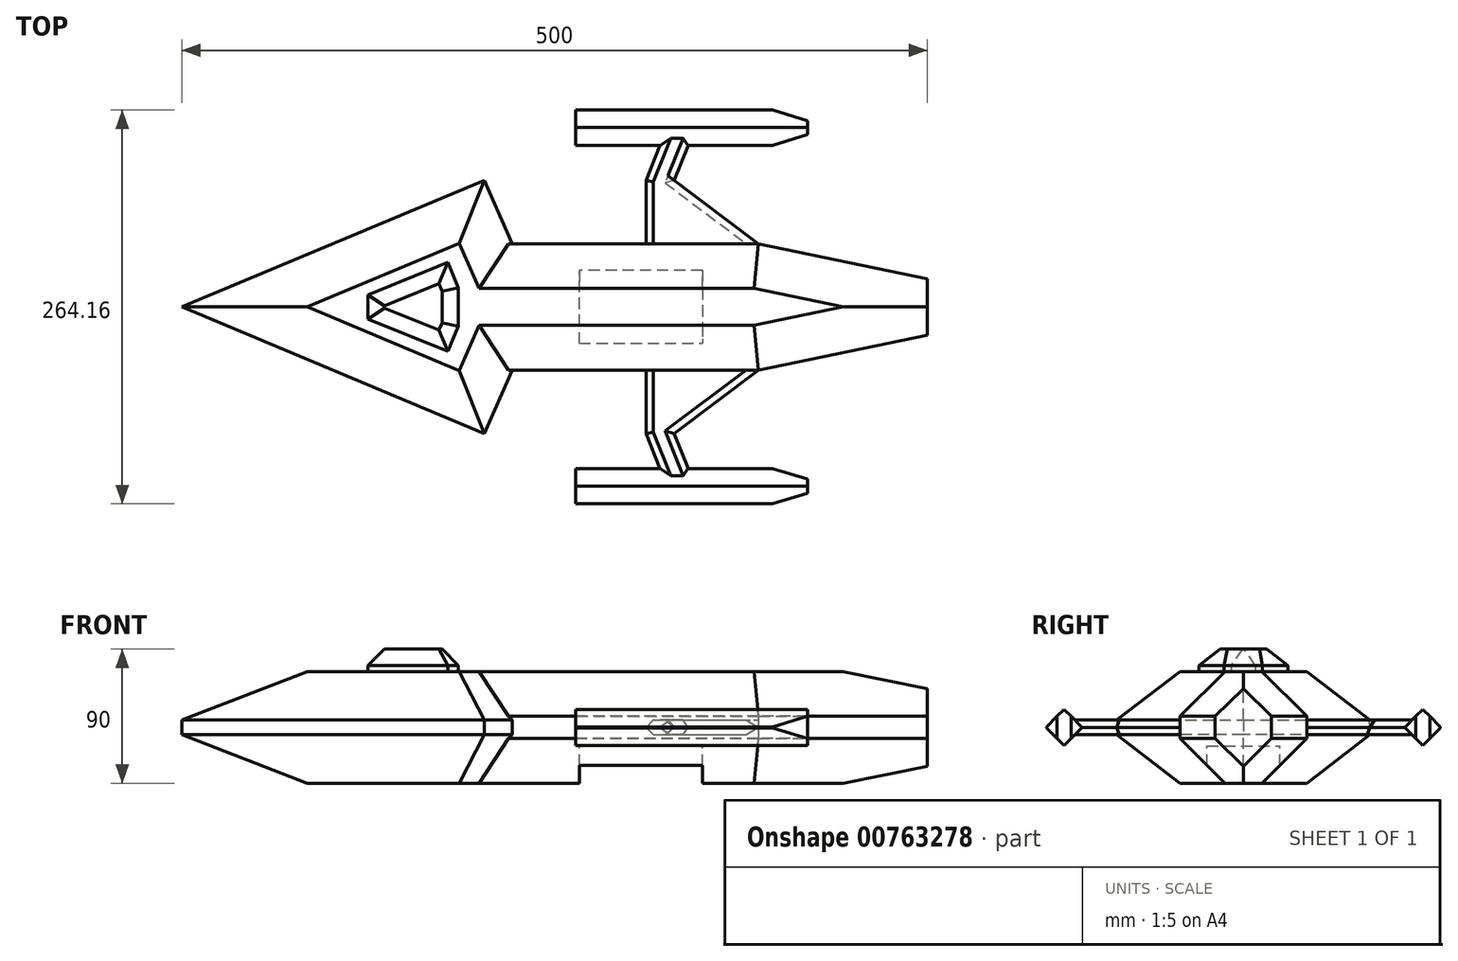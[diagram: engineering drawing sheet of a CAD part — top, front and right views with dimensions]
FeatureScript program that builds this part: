
annotation { "Feature Type Name" : "Feature", "Feature Type Description" : "" }
export const myFeature = defineFeature(function(context is Context, id is Id, definition is map)
    precondition{}
    {
        {
            var Q0;
            Q0=qCreatedBy(makeId("Top.planeOp"),FACE);
            var sketch = newSketch(context, id + "F0", { "sketchPlane" : qUnion([Q0])});
            skLineSegment(sketch, "E0", {"start": v(-309.49, 0) * mm, "end": v(-106.66, 84.9) * mm});
            skLineSegment(sketch, "E1", {"start": v(-106.66, 84.9) * mm, "end": v(-87.8, 42.45) * mm});
            skLineSegment(sketch, "E2", {"start": v(-87.8, 42.45) * mm, "end": v(1.83, 42.45) * mm});
            skLineSegment(sketch, "E3", {"start": v(1.83, 42.45) * mm, "end": v(1.83, 84.9) * mm});
            skLineSegment(sketch, "E4", {"start": v(1.83, 84.9) * mm, "end": v(11.27, 108.5) * mm});
            skLineSegment(sketch, "E5", {"start": v(11.27, 108.5) * mm, "end": v(-45.34, 108.5) * mm});
            skLineSegment(sketch, "E6", {"start": v(-45.34, 108.5) * mm, "end": v(-45.34, 132.08) * mm});
            skLineSegment(sketch, "E7", {"start": v(-45.34, 132.08) * mm, "end": v(86.74, 132.08) * mm});
            skLineSegment(sketch, "E8", {"start": v(86.74, 132.08) * mm, "end": v(110.32, 125) * mm});
            skLineSegment(sketch, "E9", {"start": v(110.32, 125) * mm, "end": v(110.32, 115.57) * mm});
            skLineSegment(sketch, "E10", {"start": v(110.32, 115.57) * mm, "end": v(86.74, 108.5) * mm});
            skLineSegment(sketch, "E11", {"start": v(86.74, 108.5) * mm, "end": v(30.13, 108.5) * mm});
            skLineSegment(sketch, "E12", {"start": v(30.13, 108.5) * mm, "end": v(20.7, 84.9) * mm});
            skLineSegment(sketch, "E13", {"start": v(20.7, 84.9) * mm, "end": v(77.3, 42.45) * mm});
            skLineSegment(sketch, "E14", {"start": v(77.3, 42.45) * mm, "end": v(190.51, 18.87) * mm});
            skLineSegment(sketch, "E15.MirrorCS", {"start": v(-309.49, 0) * mm, "end": v(-106.66, -84.9) * mm});
            skLineSegment(sketch, "E16.MirrorCS", {"start": v(-106.66, -84.9) * mm, "end": v(-87.8, -42.45) * mm});
            skLineSegment(sketch, "E17.MirrorCS", {"start": v(-87.8, -42.45) * mm, "end": v(1.83, -42.45) * mm});
            skLineSegment(sketch, "E18.MirrorCS", {"start": v(1.83, -42.45) * mm, "end": v(1.83, -84.9) * mm});
            skLineSegment(sketch, "E19.MirrorCS", {"start": v(1.83, -84.9) * mm, "end": v(11.27, -108.5) * mm});
            skLineSegment(sketch, "E20.MirrorCS", {"start": v(11.27, -108.5) * mm, "end": v(-45.34, -108.5) * mm});
            skLineSegment(sketch, "E21.MirrorCS", {"start": v(-45.34, -108.5) * mm, "end": v(-45.34, -132.08) * mm});
            skLineSegment(sketch, "E22.MirrorCS", {"start": v(-45.34, -132.08) * mm, "end": v(86.74, -132.08) * mm});
            skLineSegment(sketch, "E23.MirrorCS", {"start": v(86.74, -132.08) * mm, "end": v(110.32, -125) * mm});
            skLineSegment(sketch, "E24.MirrorCS", {"start": v(110.32, -125) * mm, "end": v(110.32, -115.57) * mm});
            skLineSegment(sketch, "E25.MirrorCS", {"start": v(110.32, -115.57) * mm, "end": v(86.74, -108.5) * mm});
            skLineSegment(sketch, "E26.MirrorCS", {"start": v(86.74, -108.5) * mm, "end": v(30.13, -108.5) * mm});
            skLineSegment(sketch, "E27.MirrorCS", {"start": v(30.13, -108.5) * mm, "end": v(20.7, -84.9) * mm});
            skLineSegment(sketch, "E28.MirrorCS", {"start": v(20.7, -84.9) * mm, "end": v(77.3, -42.45) * mm});
            skLineSegment(sketch, "E29.MirrorCS", {"start": v(77.3, -42.45) * mm, "end": v(190.51, -18.87) * mm});
            skLineSegment(sketch, "E30", {"start": v(190.51, -18.87) * mm, "end": v(190.51, 18.87) * mm});
            skPoint(sketch, "E31.endSnap0", {"position": v(98.53, 112.03) * mm});
            skPoint(sketch, "E32.startSnap0", {"position": v(-208.07, 42.45) * mm});
            skPoint(sketch, "E32.endSnap0", {"position": v(-208.07, 42.45) * mm});
            skPoint(sketch, "E33.endSnap0", {"position": v(-117.98, 30.43) * mm});
            skLineSegment(sketch, "E34", {"start": v(11.27, 108.5) * mm, "end": v(30.13, 108.5) * mm});
            skLineSegment(sketch, "E35", {"start": v(11.27, -108.5) * mm, "end": v(30.13, -108.5) * mm});
            skLineSegment(sketch, "E36", {"start": v(1.83, -42.45) * mm, "end": v(77.3, -42.45) * mm});
            skLineSegment(sketch, "E37", {"start": v(1.83, 42.45) * mm, "end": v(77.3, 42.45) * mm});
            skSolve(sketch);
        }
        {
            var Q0;
            Q0=makeQuery(id+"F0.imprint","IMPRINT",FACE,{"disambiguationData":[TD([[makeQuery(id+"F0.imprint","IMPRINT",EDGE,{"derivedFrom":sQuery(id+"F0.wireOp",EDGE,"E33")}),-1.0]])]});
            var Q1;
            Q1=makeQuery(id+"F0.imprint","IMPRINT",FACE,{"disambiguationData":[TD([[makeQuery(id+"F0.imprint","IMPRINT",EDGE,{"derivedFrom":sQuery(id+"F0.wireOp",EDGE,"E31")}),-1.0]])]});
            var Q2;
            Q2=makeQuery(id+"F0.imprint","IMPRINT",FACE,{"disambiguationData":[TD([[makeQuery(id+"F0.imprint","IMPRINT",EDGE,{"derivedFrom":sQuery(id+"F0.wireOp",EDGE,"E0")}),-1.0]])]});
            extrude(context, id + "F1", {"entities" : qUnion([Q0, Q1, Q2]), "depth" : 75 * mm, "offsetDistance" : 25 * mm, "symmetric" : true});
        }
        {
            var Q0;
            Q0=makeQuery(id+"F1.opExtrude","CAP_EDGE",EDGE,{"disambiguationData":[OSD([sQuery(id+"F0.wireOp",EDGE,"E0")])],"isStart":true});
            var Q1;
            Q1=makeQuery(id+"F1.opExtrude","CAP_EDGE",EDGE,{"disambiguationData":[OSD([sQuery(id+"F0.wireOp",EDGE,"E0")])],"isStart":false});
            var Q2;
            Q2=makeQuery(id+"F1.opExtrude","CAP_EDGE",EDGE,{"disambiguationData":[OSD([sQuery(id+"F0.wireOp",EDGE,"E15.MirrorCS")])],"isStart":false});
            var Q3;
            Q3=makeQuery(id+"F1.opExtrude","CAP_EDGE",EDGE,{"disambiguationData":[OSD([sQuery(id+"F0.wireOp",EDGE,"E15.MirrorCS")])],"isStart":true});
            var Q4;
            Q4=makeQuery(id+"F1.opExtrude","CAP_EDGE",EDGE,{"disambiguationData":[OSD([sQuery(id+"F0.wireOp",EDGE,"E16.MirrorCS")])],"isStart":false});
            var Q5;
            Q5=makeQuery(id+"F1.opExtrude","CAP_EDGE",EDGE,{"disambiguationData":[OSD([sQuery(id+"F0.wireOp",EDGE,"E16.MirrorCS")])],"isStart":true});
            var Q6;
            Q6=makeQuery(id+"F1.opExtrude","CAP_EDGE",EDGE,{"disambiguationData":[OSD([sQuery(id+"F0.wireOp",EDGE,"E1")])],"isStart":false});
            var Q7;
            Q7=makeQuery(id+"F1.opExtrude","CAP_EDGE",EDGE,{"disambiguationData":[OSD([sQuery(id+"F0.wireOp",EDGE,"E1")])],"isStart":true});
            chamfer(context, id + "F2", {"entities" : qUnion([Q0, Q1, Q2, Q3, Q4, Q5, Q6, Q7]), "width" : 32.5 * mm, "tangentPropagation" : true});
        }
        {
            var Q0;
            Q0=makeQuery(id+"F0.imprint","IMPRINT",FACE,{"disambiguationData":[TD([[makeQuery(id+"F0.imprint","IMPRINT",EDGE,{"derivedFrom":sQuery(id+"F0.wireOp",EDGE,"E18.MirrorCS")}),1.0]])]});
            var Q1;
            Q1=makeQuery(id+"F0.imprint","IMPRINT",FACE,{"disambiguationData":[TD([[makeQuery(id+"F0.imprint","IMPRINT",EDGE,{"derivedFrom":sQuery(id+"F0.wireOp",EDGE,"E3")}),-1.0]])]});
            extrude(context, id + "F3", {"entities" : qUnion([Q0, Q1]), "operationType" : NewBodyOperationType.ADD, "depth" : 10 * mm, "offsetDistance" : 25 * mm, "symmetric" : true});
        }
        {
            var Q0;
            Q0=makeQuery(id+"F0.imprint","IMPRINT",FACE,{"disambiguationData":[TD([[makeQuery(id+"F0.imprint","IMPRINT",EDGE,{"derivedFrom":sQuery(id+"F0.wireOp",EDGE,"E5")}),-1.0]])]});
            var Q1;
            Q1=makeQuery(id+"F0.imprint","IMPRINT",FACE,{"disambiguationData":[TD([[makeQuery(id+"F0.imprint","IMPRINT",EDGE,{"derivedFrom":sQuery(id+"F0.wireOp",EDGE,"E20.MirrorCS")}),1.0]])]});
            extrude(context, id + "F4", {"entities" : qUnion([Q0, Q1]), "operationType" : NewBodyOperationType.ADD, "depth" : 25 * mm, "offsetDistance" : 25 * mm, "symmetric" : true});
        }
        {
            var Q0;
            Q0=makeQuery(id+"F1.opExtrude","CAP_EDGE",EDGE,{"disambiguationData":[OSD([sQuery(id+"F0.wireOp",EDGE,"E14")])],"isStart":true});
            var Q1;
            Q1=makeQuery(id+"F1.opExtrude","CAP_EDGE",EDGE,{"disambiguationData":[OSD([sQuery(id+"F0.wireOp",EDGE,"E14")])],"isStart":false});
            var Q2;
            Q2=makeQuery(id+"F1.opExtrude","CAP_EDGE",EDGE,{"disambiguationData":[OSD([sQuery(id+"F0.wireOp",EDGE,"E29.MirrorCS")])],"isStart":false});
            var Q3;
            Q3=makeQuery(id+"F1.opExtrude","CAP_EDGE",EDGE,{"disambiguationData":[OSD([sQuery(id+"F0.wireOp",EDGE,"E29.MirrorCS")])],"isStart":true});
            var Q4;
            Q4=makeQuery(id+"F1.opExtrude","CAP_EDGE",EDGE,{"disambiguationData":[OSD([sQuery(id+"F0.wireOp",EDGE,"E17.MirrorCS"),sQuery(id+"F0.wireOp",EDGE,"E36")])],"isStart":true});
            var Q5;
            Q5=makeQuery(id+"F1.opExtrude","CAP_EDGE",EDGE,{"disambiguationData":[OSD([sQuery(id+"F0.wireOp",EDGE,"E17.MirrorCS"),sQuery(id+"F0.wireOp",EDGE,"E36")])],"isStart":false});
            var Q6;
            Q6=makeQuery(id+"F1.opExtrude","CAP_EDGE",EDGE,{"disambiguationData":[OSD([sQuery(id+"F0.wireOp",EDGE,"E2"),sQuery(id+"F0.wireOp",EDGE,"E37")])],"isStart":true});
            var Q7;
            Q7=makeQuery(id+"F1.opExtrude","CAP_EDGE",EDGE,{"disambiguationData":[OSD([sQuery(id+"F0.wireOp",EDGE,"E2"),sQuery(id+"F0.wireOp",EDGE,"E37")])],"isStart":false});
            chamfer(context, id + "F5", {"entities" : qUnion([Q0, Q1, Q2, Q3, Q4, Q5, Q6, Q7]), "width" : 30 * mm, "tangentPropagation" : true});
        }
        {
            var Q0;
            Q0=makeQuery(id+"F3.opExtrude","CAP_EDGE",EDGE,{"disambiguationData":[OSD([sQuery(id+"F0.wireOp",EDGE,"E3")])],"isStart":false});
            var Q1;
            Q1=makeQuery(id+"F3.opExtrude","CAP_EDGE",EDGE,{"disambiguationData":[OSD([sQuery(id+"F0.wireOp",EDGE,"E3")])],"isStart":true});
            var Q2;
            Q2=makeQuery(id+"F3.opExtrude","CAP_EDGE",EDGE,{"disambiguationData":[OSD([sQuery(id+"F0.wireOp",EDGE,"E13")])],"isStart":true});
            var Q3;
            Q3=makeQuery(id+"F3.opExtrude","CAP_EDGE",EDGE,{"disambiguationData":[OSD([sQuery(id+"F0.wireOp",EDGE,"E4")])],"isStart":false});
            var Q4;
            Q4=makeQuery(id+"F3.opExtrude","CAP_EDGE",EDGE,{"disambiguationData":[OSD([sQuery(id+"F0.wireOp",EDGE,"E4")])],"isStart":true});
            var Q5;
            Q5=makeQuery(id+"F3.opExtrude","CAP_EDGE",EDGE,{"disambiguationData":[OSD([sQuery(id+"F0.wireOp",EDGE,"E12")])],"isStart":true});
            var Q6;
            Q6=makeQuery(id+"F3.opExtrude","CAP_EDGE",EDGE,{"disambiguationData":[OSD([sQuery(id+"F0.wireOp",EDGE,"E12")])],"isStart":false});
            var Q7;
            Q7=makeQuery(id+"F3.opExtrude","CAP_EDGE",EDGE,{"disambiguationData":[OSD([sQuery(id+"F0.wireOp",EDGE,"E28.MirrorCS")])],"isStart":true});
            var Q8;
            Q8=makeQuery(id+"F3.opExtrude","CAP_EDGE",EDGE,{"disambiguationData":[OSD([sQuery(id+"F0.wireOp",EDGE,"E18.MirrorCS")])],"isStart":true});
            var Q9;
            Q9=makeQuery(id+"F3.opExtrude","CAP_EDGE",EDGE,{"disambiguationData":[OSD([sQuery(id+"F0.wireOp",EDGE,"E19.MirrorCS")])],"isStart":true});
            var Q10;
            Q10=makeQuery(id+"F3.opExtrude","CAP_EDGE",EDGE,{"disambiguationData":[OSD([sQuery(id+"F0.wireOp",EDGE,"E27.MirrorCS")])],"isStart":true});
            var Q11;
            Q11=makeQuery(id+"F3.opExtrude","CAP_EDGE",EDGE,{"disambiguationData":[OSD([sQuery(id+"F0.wireOp",EDGE,"E18.MirrorCS")])],"isStart":false});
            var Q12;
            Q12=makeQuery(id+"F3.opExtrude","CAP_EDGE",EDGE,{"disambiguationData":[OSD([sQuery(id+"F0.wireOp",EDGE,"E19.MirrorCS")])],"isStart":false});
            var Q13;
            Q13=makeQuery(id+"F3.opExtrude","CAP_EDGE",EDGE,{"disambiguationData":[OSD([sQuery(id+"F0.wireOp",EDGE,"E28.MirrorCS")])],"isStart":false});
            var Q14;
            Q14=makeQuery(id+"F3.opExtrude","CAP_EDGE",EDGE,{"disambiguationData":[OSD([sQuery(id+"F0.wireOp",EDGE,"E27.MirrorCS")])],"isStart":false});
            chamfer(context, id + "F6", {"entities" : qUnion([Q0, Q1, Q2, Q3, Q4, Q5, Q6, Q7, Q8, Q9, Q10, Q11, Q12, Q13, Q14]), "width" : 5 * mm, "tangentPropagation" : true});
        }
        {
            var Q0;
            Q0=makeQuery(id+"F4.opExtrude","CAP_EDGE",EDGE,{"disambiguationData":[OSD([sQuery(id+"F0.wireOp",EDGE,"E22.MirrorCS")])],"isStart":false});
            var Q1;
            Q1=makeQuery(id+"F4.opExtrude","CAP_EDGE",EDGE,{"disambiguationData":[OSD([sQuery(id+"F0.wireOp",EDGE,"E20.MirrorCS"),sQuery(id+"F0.wireOp",EDGE,"E26.MirrorCS"),sQuery(id+"F0.wireOp",EDGE,"E35")])],"isStart":false});
            var Q2;
            Q2=makeQuery(id+"F4.opExtrude","CAP_EDGE",EDGE,{"disambiguationData":[OSD([sQuery(id+"F0.wireOp",EDGE,"E22.MirrorCS")])],"isStart":true});
            var Q3;
            Q3=makeQuery(id+"F4.opExtrude","CAP_EDGE",EDGE,{"disambiguationData":[OSD([sQuery(id+"F0.wireOp",EDGE,"E20.MirrorCS"),sQuery(id+"F0.wireOp",EDGE,"E26.MirrorCS"),sQuery(id+"F0.wireOp",EDGE,"E35")])],"isStart":true});
            var Q4;
            Q4=makeQuery(id+"F4.opExtrude","CAP_EDGE",EDGE,{"disambiguationData":[OSD([sQuery(id+"F0.wireOp",EDGE,"E7")])],"isStart":true});
            var Q5;
            Q5=makeQuery(id+"F4.opExtrude","CAP_EDGE",EDGE,{"disambiguationData":[OSD([sQuery(id+"F0.wireOp",EDGE,"E7")])],"isStart":false});
            var Q6;
            Q6=makeQuery(id+"F4.opExtrude","CAP_EDGE",EDGE,{"disambiguationData":[OSD([sQuery(id+"F0.wireOp",EDGE,"E5"),sQuery(id+"F0.wireOp",EDGE,"E11"),sQuery(id+"F0.wireOp",EDGE,"E34")])],"isStart":false});
            var Q7;
            Q7=makeQuery(id+"F4.opExtrude","CAP_EDGE",EDGE,{"disambiguationData":[OSD([sQuery(id+"F0.wireOp",EDGE,"E5"),sQuery(id+"F0.wireOp",EDGE,"E11"),sQuery(id+"F0.wireOp",EDGE,"E34")])],"isStart":true});
            chamfer(context, id + "F7", {"entities" : qUnion([Q0, Q1, Q2, Q3, Q4, Q5, Q6, Q7]), "width" : 12.2 * mm, "tangentPropagation" : true});
        }
        {
            var Q0;
            Q0=qCreatedBy(makeId("Top.planeOp"),FACE);
            cPlane(context, id + "F8", {"entities" : qUnion([Q0]), "cplaneType" : CPlaneType.OFFSET, "offset" : 37.5 * mm, "width" : 150 * mm, "height" : 150 * mm});
        }
        {
            var Q0;
            Q0=qCreatedBy(id+"F8.planeOp",FACE);
            var sketch = newSketch(context, id + "F9", { "sketchPlane" : qUnion([Q0])});
            skLineSegment(sketch, "E38", {"start": v(-184.6, -8.14) * mm, "end": v(-130.94, -29.85) * mm});
            skLineSegment(sketch, "E39", {"start": v(-130.94, -29.85) * mm, "end": v(-124.05, -12.82) * mm});
            skLineSegment(sketch, "E40.MirrorCS", {"start": v(-130.94, 29.85) * mm, "end": v(-124.05, 12.82) * mm});
            skLineSegment(sketch, "E41.MirrorCS", {"start": v(-184.6, 8.14) * mm, "end": v(-130.94, 29.85) * mm});
            skLineSegment(sketch, "E42", {"start": v(-184.6, -8.14) * mm, "end": v(-184.6, 8.14) * mm});
            skLineSegment(sketch, "E43", {"start": v(-124.05, -12.82) * mm, "end": v(-124.05, 12.82) * mm});
            skSolve(sketch);
        }
        {
            var Q0;
            Q0=makeQuery(id+"F9.imprint","IMPRINT",FACE,{"disambiguationData":[TD([[makeQuery(id+"F9.imprint","IMPRINT",EDGE,{"derivedFrom":sQuery(id+"F9.wireOp",EDGE,"E38")}),1.0]])]});
            extrude(context, id + "F10", {"entities" : qUnion([Q0]), "operationType" : NewBodyOperationType.ADD, "depth" : 15 * mm, "offsetDistance" : 25 * mm});
        }
        {
            var Q0;
            Q0=makeQuery(id+"F10.opExtrude","CAP_FACE",FACE,{"disambiguationData":[OSD([sQuery(id+"F9.wireOp",EDGE,"E38"),sQuery(id+"F9.wireOp",EDGE,"E39"),sQuery(id+"F9.wireOp",EDGE,"E40.MirrorCS"),sQuery(id+"F9.wireOp",EDGE,"E41.MirrorCS"),sQuery(id+"F9.wireOp",EDGE,"E42"),sQuery(id+"F9.wireOp",EDGE,"E43")])],"isStart":false});
            chamfer(context, id + "F11", {"entities" : qUnion([Q0]), "width" : 11 * mm, "tangentPropagation" : true});
        }
        {
            var Q0;
            Q0=qCreatedBy(makeId("Top.planeOp"),FACE);
            cPlane(context, id + "F12", {"entities" : qUnion([Q0]), "cplaneType" : CPlaneType.OFFSET, "offset" : 12.5 * mm, "oppositeDirection" : true, "width" : 150 * mm, "height" : 150 * mm});
        }
        {
            var Q0;
            Q0=qCreatedBy(id+"F12.planeOp",FACE);
            var sketch = newSketch(context, id + "F13", { "sketchPlane" : qUnion([Q0])});
            skLineSegment(sketch, "E44", {"start": v(-42.9, 24.42) * mm, "end": v(39.7, 24.42) * mm});
            skLineSegment(sketch, "E45.MirrorCS", {"start": v(-42.9, -24.42) * mm, "end": v(39.7, -24.42) * mm});
            skLineSegment(sketch, "E46", {"start": v(-42.9, -24.42) * mm, "end": v(-42.9, 24.42) * mm});
            skLineSegment(sketch, "E47", {"start": v(39.7, 24.42) * mm, "end": v(39.7, -24.42) * mm});
            skSolve(sketch);
        }
        {
            var Q0;
            Q0 = qSketchRegion(id + "F13", true);
            extrude(context, id + "F14", {"entities" : qUnion([Q0]), "operationType" : NewBodyOperationType.REMOVE, "oppositeDirection" : true, "depth" : 25 * mm, "offsetDistance" : 25 * mm});
        }
    });
